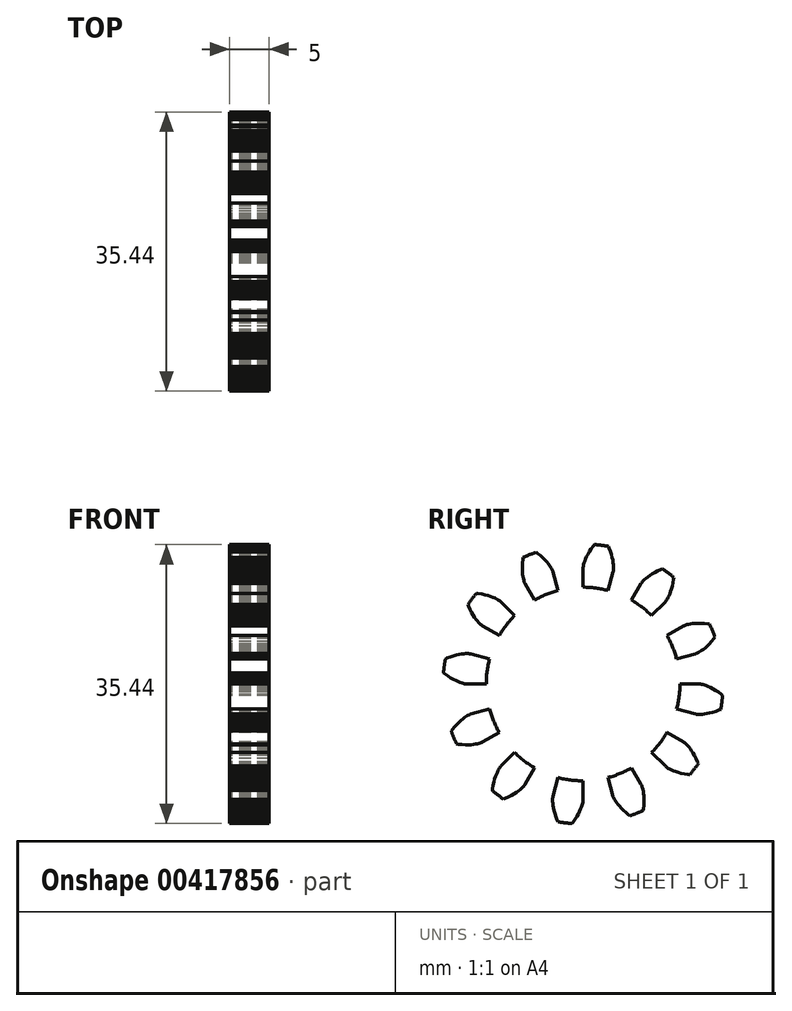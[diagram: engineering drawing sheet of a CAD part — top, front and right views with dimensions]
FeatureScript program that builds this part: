
annotation { "Feature Type Name" : "Feature", "Feature Type Description" : "" }
export const myFeature = defineFeature(function(context is Context, id is Id, definition is map)
    precondition{}
    {
        {
            assignVariable(context, id + "F0", {"name" : "GearThickness", "anyValue" : 5});
        }
        {
            var Q0;
            Q0=qCreatedBy(makeId("Right.planeOp"),FACE);
            var sketch = newSketch(context, id + "F1", { "sketchPlane" : qUnion([Q0])});
            skCircle(sketch, "E0", {"center": v(0, 0) * mm, "radius": 12.3 * mm});
            skCircle(sketch, "E1", {"center": v(0, 0) * mm, "radius": 14.75 * mm, "construction": true});
            skCircle(sketch, "E2", {"center": v(0, 0) * mm, "radius": 15.24 * mm, "construction": true});
            skCircle(sketch, "E3", {"center": v(0, 0) * mm, "radius": 17.78 * mm});
            skLineSegment(sketch, "E4", {"start": v(0, 0) * mm, "end": v(-14.75, 0) * mm, "construction": true});
            skLineSegment(sketch, "E5.1.0", {"start": v(0, 0) * mm, "end": v(-14.74, 0.74) * mm, "construction": true});
            skLineSegment(sketch, "E5.2.0", {"start": v(0, 0) * mm, "end": v(-14.68, 1.47) * mm, "construction": true});
            skLineSegment(sketch, "E5.3.0", {"start": v(0, 0) * mm, "end": v(-14.59, 2.2) * mm, "construction": true});
            skLineSegment(sketch, "E5.4.0", {"start": v(0, 0) * mm, "end": v(-14.46, 2.93) * mm, "construction": true});
            skLineSegment(sketch, "E5.5.0", {"start": v(0, 0) * mm, "end": v(-14.3, 3.65) * mm, "construction": true});
            skLineSegment(sketch, "E5.6.0", {"start": v(0, 0) * mm, "end": v(-14.1, 4.36) * mm, "construction": true});
            skLineSegment(sketch, "E5.7.0", {"start": v(0, 0) * mm, "end": v(-13.86, 5.06) * mm, "construction": true});
            skLineSegment(sketch, "E5.8.0", {"start": v(0, 0) * mm, "end": v(-13.59, 5.75) * mm, "construction": true});
            skLineSegment(sketch, "E5.9.0", {"start": v(0, 0) * mm, "end": v(-13.29, 6.42) * mm, "construction": true});
            skLineSegment(sketch, "E5.10.0", {"start": v(0, 0) * mm, "end": v(-12.95, 7.07) * mm, "construction": true});
            skLineSegment(sketch, "E5.11.0", {"start": v(0, 0) * mm, "end": v(-12.58, 7.71) * mm, "construction": true});
            skLineSegment(sketch, "E5.12.0", {"start": v(0, 0) * mm, "end": v(-12.18, 8.33) * mm, "construction": true});
            skLineSegment(sketch, "E5.13.0", {"start": v(0, 0) * mm, "end": v(-11.75, 8.93) * mm, "construction": true});
            skLineSegment(sketch, "E5.14.0", {"start": v(0, 0) * mm, "end": v(-11.28, 9.5) * mm, "construction": true});
            skLineSegment(sketch, "E5.anchor2", {"start": v(0, 0) * mm, "end": v(-11.28, 9.5) * mm, "construction": true});
            skLineSegment(sketch, "E6", {"start": v(-14.74, 0.74) * mm, "end": v(-14.77, 0) * mm, "construction": true});
            skLineSegment(sketch, "E7", {"start": v(-14.68, 1.47) * mm, "end": v(-14.83, 0) * mm, "construction": true});
            skLineSegment(sketch, "E8", {"start": v(-14.59, 2.2) * mm, "end": v(-14.92, 0.02) * mm, "construction": true});
            skLineSegment(sketch, "E9", {"start": v(-14.3, 3.65) * mm, "end": v(-15.2, 0.08) * mm, "construction": true});
            skLineSegment(sketch, "E10", {"start": v(-14.1, 4.36) * mm, "end": v(-15.4, 0.13) * mm, "construction": true});
            skLineSegment(sketch, "E11", {"start": v(-13.86, 5.06) * mm, "end": v(-15.63, 0.2) * mm, "construction": true});
            skLineSegment(sketch, "E12", {"start": v(-13.59, 5.75) * mm, "end": v(-15.89, 0.3) * mm, "construction": true});
            skLineSegment(sketch, "E13", {"start": v(-13.29, 6.42) * mm, "end": v(-16.17, 0.44) * mm, "construction": true});
            skLineSegment(sketch, "E14", {"start": v(-12.95, 7.07) * mm, "end": v(-16.49, 0.6) * mm, "construction": true});
            skLineSegment(sketch, "E15", {"start": v(-12.58, 7.71) * mm, "end": v(-16.82, 0.8) * mm, "construction": true});
            skLineSegment(sketch, "E16", {"start": v(-14.46, 2.93) * mm, "end": v(-15.05, 0.04) * mm, "construction": true});
            skLineSegment(sketch, "E17", {"start": v(-12.18, 8.33) * mm, "end": v(-17.18, 1.02) * mm, "construction": true});
            skLineSegment(sketch, "E18", {"start": v(-11.75, 8.93) * mm, "end": v(-17.55, 1.3) * mm, "construction": true});
            skLineSegment(sketch, "E19", {"start": v(-11.28, 9.5) * mm, "end": v(-17.94, 1.6) * mm, "construction": true});
            skLineSegment(sketch, "E20", {"start": v(0, 0) * mm, "end": v(-14.63, 1.93) * mm, "construction": true});
            skLineSegment(sketch, "E21", {"start": v(-12.3, 0) * mm, "end": v(-14.75, 0) * mm});
            skLineSegment(sketch, "E22.MirrorCS", {"start": v(-11.88, 3.18) * mm, "end": v(-14.25, 3.82) * mm});
            skLineSegment(sketch, "E23", {"start": v(-14.75, 0) * mm, "end": v(-14.77, 0) * mm});
            skLineSegment(sketch, "E24", {"start": v(-14.77, 0) * mm, "end": v(-14.83, 0) * mm});
            skLineSegment(sketch, "E25", {"start": v(-14.83, 0) * mm, "end": v(-14.92, 0.02) * mm});
            skLineSegment(sketch, "E26", {"start": v(-14.92, 0.02) * mm, "end": v(-15.05, 0.04) * mm});
            skLineSegment(sketch, "E27", {"start": v(-15.05, 0.04) * mm, "end": v(-15.2, 0.08) * mm});
            skLineSegment(sketch, "E28", {"start": v(-15.2, 0.08) * mm, "end": v(-15.4, 0.13) * mm});
            skLineSegment(sketch, "E29", {"start": v(-15.4, 0.13) * mm, "end": v(-15.63, 0.2) * mm});
            skLineSegment(sketch, "E30", {"start": v(-15.63, 0.2) * mm, "end": v(-15.89, 0.3) * mm});
            skLineSegment(sketch, "E31", {"start": v(-15.89, 0.3) * mm, "end": v(-16.17, 0.44) * mm});
            skLineSegment(sketch, "E32", {"start": v(-16.17, 0.44) * mm, "end": v(-16.49, 0.6) * mm});
            skLineSegment(sketch, "E33", {"start": v(-16.49, 0.6) * mm, "end": v(-16.82, 0.8) * mm});
            skLineSegment(sketch, "E34", {"start": v(-16.82, 0.8) * mm, "end": v(-17.18, 1.02) * mm});
            skLineSegment(sketch, "E35", {"start": v(-17.18, 1.02) * mm, "end": v(-17.55, 1.3) * mm});
            skLineSegment(sketch, "E36", {"start": v(-17.55, 1.3) * mm, "end": v(-17.94, 1.6) * mm});
            skLineSegment(sketch, "E37.MirrorCS", {"start": v(-14.25, 3.82) * mm, "end": v(-14.27, 3.82) * mm});
            skLineSegment(sketch, "E38.MirrorCS", {"start": v(-14.27, 3.82) * mm, "end": v(-14.32, 3.83) * mm});
            skLineSegment(sketch, "E39.MirrorCS", {"start": v(-14.32, 3.83) * mm, "end": v(-14.42, 3.85) * mm});
            skLineSegment(sketch, "E40.MirrorCS", {"start": v(-14.42, 3.85) * mm, "end": v(-14.54, 3.86) * mm});
            skLineSegment(sketch, "E41.MirrorCS", {"start": v(-14.71, 3.86) * mm, "end": v(-14.91, 3.86) * mm});
            skLineSegment(sketch, "E42.MirrorCS", {"start": v(-14.91, 3.86) * mm, "end": v(-15.15, 3.84) * mm});
            skLineSegment(sketch, "E43.MirrorCS", {"start": v(-15.15, 3.84) * mm, "end": v(-15.43, 3.81) * mm});
            skLineSegment(sketch, "E44.MirrorCS", {"start": v(-15.43, 3.81) * mm, "end": v(-15.74, 3.76) * mm});
            skLineSegment(sketch, "E45.MirrorCS", {"start": v(-16.08, 3.69) * mm, "end": v(-16.45, 3.59) * mm});
            skLineSegment(sketch, "E46.MirrorCS", {"start": v(-15.74, 3.76) * mm, "end": v(-16.08, 3.69) * mm});
            skLineSegment(sketch, "E47.MirrorCS", {"start": v(-16.45, 3.59) * mm, "end": v(-16.86, 3.46) * mm});
            skLineSegment(sketch, "E48.MirrorCS", {"start": v(-16.86, 3.46) * mm, "end": v(-17.29, 3.3) * mm});
            skLineSegment(sketch, "E49.MirrorCS", {"start": v(-17.29, 3.3) * mm, "end": v(-17.74, 3.1) * mm});
            skLineSegment(sketch, "E50.MirrorCS", {"start": v(-14.54, 3.86) * mm, "end": v(-14.71, 3.86) * mm});
            skLineSegment(sketch, "E51.1.0", {"start": v(-10.65, -6.15) * mm, "end": v(-12.78, -7.38) * mm});
            skLineSegment(sketch, "E51.1.1", {"start": v(-16.04, -5.12) * mm, "end": v(-16.33, -5.44) * mm});
            skLineSegment(sketch, "E51.1.2", {"start": v(-11.88, -3.18) * mm, "end": v(-14.25, -3.82) * mm});
            skLineSegment(sketch, "E51.1.3", {"start": v(-15.77, -4.85) * mm, "end": v(-16.04, -5.12) * mm});
            skLineSegment(sketch, "E51.1.4", {"start": v(-14.58, -7.72) * mm, "end": v(-14.96, -7.72) * mm});
            skLineSegment(sketch, "E51.1.5", {"start": v(-14.96, -7.72) * mm, "end": v(-15.39, -7.7) * mm});
            skLineSegment(sketch, "E51.1.6", {"start": v(-15.5, -4.61) * mm, "end": v(-15.77, -4.85) * mm});
            skLineSegment(sketch, "E51.1.7", {"start": v(-16.62, -5.8) * mm, "end": v(-16.91, -6.2) * mm});
            skLineSegment(sketch, "E51.1.8", {"start": v(-15.27, -4.41) * mm, "end": v(-15.5, -4.61) * mm});
            skLineSegment(sketch, "E51.1.9", {"start": v(-15.85, -7.65) * mm, "end": v(-16.34, -7.58) * mm});
            skLineSegment(sketch, "E51.1.10", {"start": v(-16.33, -5.44) * mm, "end": v(-16.62, -5.8) * mm});
            skLineSegment(sketch, "E51.1.11", {"start": v(-14.23, -7.7) * mm, "end": v(-14.58, -7.72) * mm});
            skLineSegment(sketch, "E51.1.12", {"start": v(-15.39, -7.7) * mm, "end": v(-15.85, -7.65) * mm});
            skLineSegment(sketch, "E51.1.13", {"start": v(-14.67, -4.01) * mm, "end": v(-14.84, -4.11) * mm});
            skLineSegment(sketch, "E51.1.14", {"start": v(-14.84, -4.11) * mm, "end": v(-15.04, -4.25) * mm});
            skLineSegment(sketch, "E51.1.15", {"start": v(-15.04, -4.25) * mm, "end": v(-15.27, -4.41) * mm});
            skLineSegment(sketch, "E51.1.16", {"start": v(-13.64, -7.64) * mm, "end": v(-13.91, -7.68) * mm});
            skLineSegment(sketch, "E51.1.17", {"start": v(-13.4, -7.59) * mm, "end": v(-13.64, -7.64) * mm});
            skLineSegment(sketch, "E51.1.18", {"start": v(-13.91, -7.68) * mm, "end": v(-14.23, -7.7) * mm});
            skLineSegment(sketch, "E51.1.19", {"start": v(-14.52, -3.93) * mm, "end": v(-14.67, -4.01) * mm});
            skLineSegment(sketch, "E51.1.20", {"start": v(-14.4, -3.88) * mm, "end": v(-14.52, -3.93) * mm});
            skLineSegment(sketch, "E51.1.21", {"start": v(-13.2, -7.54) * mm, "end": v(-13.4, -7.59) * mm});
            skLineSegment(sketch, "E51.1.22", {"start": v(-13.05, -7.49) * mm, "end": v(-13.2, -7.54) * mm});
            skLineSegment(sketch, "E51.1.23", {"start": v(-12.84, -7.4) * mm, "end": v(-12.93, -7.45) * mm});
            skLineSegment(sketch, "E51.1.24", {"start": v(-14.25, -3.82) * mm, "end": v(-14.27, -3.82) * mm});
            skLineSegment(sketch, "E51.1.25", {"start": v(-14.27, -3.82) * mm, "end": v(-14.32, -3.84) * mm});
            skLineSegment(sketch, "E51.1.26", {"start": v(-12.93, -7.45) * mm, "end": v(-13.05, -7.49) * mm});
            skLineSegment(sketch, "E51.1.27", {"start": v(-14.32, -3.84) * mm, "end": v(-14.4, -3.88) * mm});
            skLineSegment(sketch, "E51.1.28", {"start": v(-12.8, -7.39) * mm, "end": v(-12.84, -7.4) * mm});
            skLineSegment(sketch, "E51.1.29", {"start": v(-12.78, -7.38) * mm, "end": v(-12.8, -7.39) * mm});
            skLineSegment(sketch, "E51.2.0", {"start": v(-6.15, -10.65) * mm, "end": v(-7.38, -12.78) * mm});
            skLineSegment(sketch, "E51.2.1", {"start": v(-11.33, -12.45) * mm, "end": v(-11.42, -12.87) * mm});
            skLineSegment(sketch, "E51.2.2", {"start": v(-8.7, -8.7) * mm, "end": v(-10.43, -10.43) * mm});
            skLineSegment(sketch, "E51.2.3", {"start": v(-11.23, -12.08) * mm, "end": v(-11.33, -12.45) * mm});
            skLineSegment(sketch, "E51.2.4", {"start": v(-8.76, -13.98) * mm, "end": v(-9.1, -14.17) * mm});
            skLineSegment(sketch, "E51.2.5", {"start": v(-9.1, -14.17) * mm, "end": v(-9.48, -14.36) * mm});
            skLineSegment(sketch, "E51.2.6", {"start": v(-11.13, -11.75) * mm, "end": v(-11.23, -12.08) * mm});
            skLineSegment(sketch, "E51.2.7", {"start": v(-11.5, -13.32) * mm, "end": v(-11.55, -13.82) * mm});
            skLineSegment(sketch, "E51.2.8", {"start": v(-11.02, -11.45) * mm, "end": v(-11.13, -11.75) * mm});
            skLineSegment(sketch, "E51.2.9", {"start": v(-9.9, -14.55) * mm, "end": v(-10.36, -14.73) * mm});
            skLineSegment(sketch, "E51.2.10", {"start": v(-11.42, -12.87) * mm, "end": v(-11.5, -13.32) * mm});
            skLineSegment(sketch, "E51.2.11", {"start": v(-8.47, -13.79) * mm, "end": v(-8.76, -13.98) * mm});
            skLineSegment(sketch, "E51.2.12", {"start": v(-9.48, -14.36) * mm, "end": v(-9.9, -14.55) * mm});
            skLineSegment(sketch, "E51.2.13", {"start": v(-10.7, -10.8) * mm, "end": v(-10.8, -10.99) * mm});
            skLineSegment(sketch, "E51.2.14", {"start": v(-10.8, -10.99) * mm, "end": v(-10.9, -11.2) * mm});
            skLineSegment(sketch, "E51.2.15", {"start": v(-10.9, -11.2) * mm, "end": v(-11.02, -11.45) * mm});
            skLineSegment(sketch, "E51.2.16", {"start": v(-8, -13.43) * mm, "end": v(-8.21, -13.6) * mm});
            skLineSegment(sketch, "E51.2.17", {"start": v(-7.82, -13.27) * mm, "end": v(-8, -13.43) * mm});
            skLineSegment(sketch, "E51.2.18", {"start": v(-8.21, -13.6) * mm, "end": v(-8.47, -13.79) * mm});
            skLineSegment(sketch, "E51.2.19", {"start": v(-10.61, -10.67) * mm, "end": v(-10.7, -10.8) * mm});
            skLineSegment(sketch, "E51.2.20", {"start": v(-10.54, -10.56) * mm, "end": v(-10.61, -10.67) * mm});
            skLineSegment(sketch, "E51.2.21", {"start": v(-7.67, -13.13) * mm, "end": v(-7.82, -13.27) * mm});
            skLineSegment(sketch, "E51.2.22", {"start": v(-7.56, -13.01) * mm, "end": v(-7.67, -13.13) * mm});
            skLineSegment(sketch, "E51.2.23", {"start": v(-7.42, -12.84) * mm, "end": v(-7.47, -12.91) * mm});
            skLineSegment(sketch, "E51.2.24", {"start": v(-10.43, -10.43) * mm, "end": v(-10.45, -10.45) * mm});
            skLineSegment(sketch, "E51.2.25", {"start": v(-10.45, -10.45) * mm, "end": v(-10.48, -10.49) * mm});
            skLineSegment(sketch, "E51.2.26", {"start": v(-7.47, -12.91) * mm, "end": v(-7.56, -13.01) * mm});
            skLineSegment(sketch, "E51.2.27", {"start": v(-10.48, -10.49) * mm, "end": v(-10.54, -10.56) * mm});
            skLineSegment(sketch, "E51.2.28", {"start": v(-7.39, -12.8) * mm, "end": v(-7.42, -12.84) * mm});
            skLineSegment(sketch, "E51.2.29", {"start": v(-7.38, -12.78) * mm, "end": v(-7.39, -12.8) * mm});
            skLineSegment(sketch, "E51.3.0", {"start": v(0, -12.3) * mm, "end": v(0, -14.75) * mm});
            skLineSegment(sketch, "E51.3.1", {"start": v(-3.59, -16.45) * mm, "end": v(-3.46, -16.86) * mm});
            skLineSegment(sketch, "E51.3.2", {"start": v(-3.18, -11.88) * mm, "end": v(-3.82, -14.25) * mm});
            skLineSegment(sketch, "E51.3.3", {"start": v(-3.69, -16.08) * mm, "end": v(-3.59, -16.45) * mm});
            skLineSegment(sketch, "E51.3.4", {"start": v(-0.6, -16.49) * mm, "end": v(-0.8, -16.82) * mm});
            skLineSegment(sketch, "E51.3.5", {"start": v(-0.8, -16.82) * mm, "end": v(-1.02, -17.18) * mm});
            skLineSegment(sketch, "E51.3.6", {"start": v(-3.76, -15.74) * mm, "end": v(-3.69, -16.08) * mm});
            skLineSegment(sketch, "E51.3.7", {"start": v(-3.3, -17.29) * mm, "end": v(-3.1, -17.74) * mm});
            skLineSegment(sketch, "E51.3.8", {"start": v(-3.81, -15.43) * mm, "end": v(-3.76, -15.74) * mm});
            skLineSegment(sketch, "E51.3.9", {"start": v(-1.3, -17.55) * mm, "end": v(-1.6, -17.94) * mm});
            skLineSegment(sketch, "E51.3.10", {"start": v(-3.46, -16.86) * mm, "end": v(-3.3, -17.29) * mm});
            skLineSegment(sketch, "E51.3.11", {"start": v(-0.44, -16.17) * mm, "end": v(-0.6, -16.49) * mm});
            skLineSegment(sketch, "E51.3.12", {"start": v(-1.02, -17.18) * mm, "end": v(-1.3, -17.55) * mm});
            skLineSegment(sketch, "E51.3.13", {"start": v(-3.86, -14.71) * mm, "end": v(-3.86, -14.91) * mm});
            skLineSegment(sketch, "E51.3.14", {"start": v(-3.86, -14.91) * mm, "end": v(-3.84, -15.15) * mm});
            skLineSegment(sketch, "E51.3.15", {"start": v(-3.84, -15.15) * mm, "end": v(-3.81, -15.43) * mm});
            skLineSegment(sketch, "E51.3.16", {"start": v(-0.2, -15.63) * mm, "end": v(-0.3, -15.89) * mm});
            skLineSegment(sketch, "E51.3.17", {"start": v(-0.13, -15.4) * mm, "end": v(-0.2, -15.63) * mm});
            skLineSegment(sketch, "E51.3.18", {"start": v(-0.3, -15.89) * mm, "end": v(-0.44, -16.17) * mm});
            skLineSegment(sketch, "E51.3.19", {"start": v(-3.86, -14.54) * mm, "end": v(-3.86, -14.71) * mm});
            skLineSegment(sketch, "E51.3.20", {"start": v(-3.85, -14.42) * mm, "end": v(-3.86, -14.54) * mm});
            skLineSegment(sketch, "E51.3.21", {"start": v(-0.08, -15.2) * mm, "end": v(-0.13, -15.4) * mm});
            skLineSegment(sketch, "E51.3.22", {"start": v(-0.04, -15.05) * mm, "end": v(-0.08, -15.2) * mm});
            skLineSegment(sketch, "E51.3.23", {"start": v(0, -14.83) * mm, "end": v(-0.02, -14.92) * mm});
            skLineSegment(sketch, "E51.3.24", {"start": v(-3.82, -14.25) * mm, "end": v(-3.82, -14.27) * mm});
            skLineSegment(sketch, "E51.3.25", {"start": v(-3.82, -14.27) * mm, "end": v(-3.83, -14.32) * mm});
            skLineSegment(sketch, "E51.3.26", {"start": v(-0.02, -14.92) * mm, "end": v(-0.04, -15.05) * mm});
            skLineSegment(sketch, "E51.3.27", {"start": v(-3.83, -14.32) * mm, "end": v(-3.85, -14.42) * mm});
            skLineSegment(sketch, "E51.3.28", {"start": v(0, -14.77) * mm, "end": v(0, -14.83) * mm});
            skLineSegment(sketch, "E51.3.29", {"start": v(0, -14.75) * mm, "end": v(0, -14.77) * mm});
            skLineSegment(sketch, "E51.4.0", {"start": v(6.15, -10.65) * mm, "end": v(7.38, -12.78) * mm});
            skLineSegment(sketch, "E51.4.1", {"start": v(5.12, -16.04) * mm, "end": v(5.44, -16.33) * mm});
            skLineSegment(sketch, "E51.4.2", {"start": v(3.18, -11.88) * mm, "end": v(3.82, -14.25) * mm});
            skLineSegment(sketch, "E51.4.3", {"start": v(4.85, -15.77) * mm, "end": v(5.12, -16.04) * mm});
            skLineSegment(sketch, "E51.4.4", {"start": v(7.72, -14.58) * mm, "end": v(7.72, -14.96) * mm});
            skLineSegment(sketch, "E51.4.5", {"start": v(7.72, -14.96) * mm, "end": v(7.7, -15.39) * mm});
            skLineSegment(sketch, "E51.4.6", {"start": v(4.61, -15.5) * mm, "end": v(4.85, -15.77) * mm});
            skLineSegment(sketch, "E51.4.7", {"start": v(5.8, -16.62) * mm, "end": v(6.2, -16.91) * mm});
            skLineSegment(sketch, "E51.4.8", {"start": v(4.41, -15.27) * mm, "end": v(4.61, -15.5) * mm});
            skLineSegment(sketch, "E51.4.9", {"start": v(7.65, -15.85) * mm, "end": v(7.58, -16.34) * mm});
            skLineSegment(sketch, "E51.4.10", {"start": v(5.44, -16.33) * mm, "end": v(5.8, -16.62) * mm});
            skLineSegment(sketch, "E51.4.11", {"start": v(7.7, -14.23) * mm, "end": v(7.72, -14.58) * mm});
            skLineSegment(sketch, "E51.4.12", {"start": v(7.7, -15.39) * mm, "end": v(7.65, -15.85) * mm});
            skLineSegment(sketch, "E51.4.13", {"start": v(4.01, -14.67) * mm, "end": v(4.11, -14.84) * mm});
            skLineSegment(sketch, "E51.4.14", {"start": v(4.11, -14.84) * mm, "end": v(4.25, -15.04) * mm});
            skLineSegment(sketch, "E51.4.15", {"start": v(4.25, -15.04) * mm, "end": v(4.41, -15.27) * mm});
            skLineSegment(sketch, "E51.4.16", {"start": v(7.64, -13.64) * mm, "end": v(7.68, -13.91) * mm});
            skLineSegment(sketch, "E51.4.17", {"start": v(7.59, -13.4) * mm, "end": v(7.64, -13.64) * mm});
            skLineSegment(sketch, "E51.4.18", {"start": v(7.68, -13.91) * mm, "end": v(7.7, -14.23) * mm});
            skLineSegment(sketch, "E51.4.19", {"start": v(3.93, -14.52) * mm, "end": v(4.01, -14.67) * mm});
            skLineSegment(sketch, "E51.4.20", {"start": v(3.88, -14.4) * mm, "end": v(3.93, -14.52) * mm});
            skLineSegment(sketch, "E51.4.21", {"start": v(7.54, -13.2) * mm, "end": v(7.59, -13.4) * mm});
            skLineSegment(sketch, "E51.4.22", {"start": v(7.49, -13.05) * mm, "end": v(7.54, -13.2) * mm});
            skLineSegment(sketch, "E51.4.23", {"start": v(7.4, -12.84) * mm, "end": v(7.45, -12.93) * mm});
            skLineSegment(sketch, "E51.4.24", {"start": v(3.82, -14.25) * mm, "end": v(3.82, -14.27) * mm});
            skLineSegment(sketch, "E51.4.25", {"start": v(3.82, -14.27) * mm, "end": v(3.84, -14.32) * mm});
            skLineSegment(sketch, "E51.4.26", {"start": v(7.45, -12.93) * mm, "end": v(7.49, -13.05) * mm});
            skLineSegment(sketch, "E51.4.27", {"start": v(3.84, -14.32) * mm, "end": v(3.88, -14.4) * mm});
            skLineSegment(sketch, "E51.4.28", {"start": v(7.39, -12.8) * mm, "end": v(7.4, -12.84) * mm});
            skLineSegment(sketch, "E51.4.29", {"start": v(7.38, -12.78) * mm, "end": v(7.39, -12.8) * mm});
            skLineSegment(sketch, "E51.5.0", {"start": v(10.65, -6.15) * mm, "end": v(12.78, -7.38) * mm});
            skLineSegment(sketch, "E51.5.1", {"start": v(12.45, -11.33) * mm, "end": v(12.87, -11.42) * mm});
            skLineSegment(sketch, "E51.5.2", {"start": v(8.7, -8.7) * mm, "end": v(10.43, -10.43) * mm});
            skLineSegment(sketch, "E51.5.3", {"start": v(12.08, -11.23) * mm, "end": v(12.45, -11.33) * mm});
            skLineSegment(sketch, "E51.5.4", {"start": v(13.98, -8.76) * mm, "end": v(14.17, -9.1) * mm});
            skLineSegment(sketch, "E51.5.5", {"start": v(14.17, -9.1) * mm, "end": v(14.36, -9.48) * mm});
            skLineSegment(sketch, "E51.5.6", {"start": v(11.75, -11.13) * mm, "end": v(12.08, -11.23) * mm});
            skLineSegment(sketch, "E51.5.7", {"start": v(13.32, -11.5) * mm, "end": v(13.82, -11.55) * mm});
            skLineSegment(sketch, "E51.5.8", {"start": v(11.45, -11.02) * mm, "end": v(11.75, -11.13) * mm});
            skLineSegment(sketch, "E51.5.9", {"start": v(14.55, -9.9) * mm, "end": v(14.73, -10.36) * mm});
            skLineSegment(sketch, "E51.5.10", {"start": v(12.87, -11.42) * mm, "end": v(13.32, -11.5) * mm});
            skLineSegment(sketch, "E51.5.11", {"start": v(13.79, -8.47) * mm, "end": v(13.98, -8.76) * mm});
            skLineSegment(sketch, "E51.5.12", {"start": v(14.36, -9.48) * mm, "end": v(14.55, -9.9) * mm});
            skLineSegment(sketch, "E51.5.13", {"start": v(10.8, -10.7) * mm, "end": v(10.99, -10.8) * mm});
            skLineSegment(sketch, "E51.5.14", {"start": v(10.99, -10.8) * mm, "end": v(11.2, -10.9) * mm});
            skLineSegment(sketch, "E51.5.15", {"start": v(11.2, -10.9) * mm, "end": v(11.45, -11.02) * mm});
            skLineSegment(sketch, "E51.5.16", {"start": v(13.43, -8) * mm, "end": v(13.6, -8.21) * mm});
            skLineSegment(sketch, "E51.5.17", {"start": v(13.27, -7.82) * mm, "end": v(13.43, -8) * mm});
            skLineSegment(sketch, "E51.5.18", {"start": v(13.6, -8.21) * mm, "end": v(13.79, -8.47) * mm});
            skLineSegment(sketch, "E51.5.19", {"start": v(10.67, -10.61) * mm, "end": v(10.8, -10.7) * mm});
            skLineSegment(sketch, "E51.5.20", {"start": v(10.56, -10.54) * mm, "end": v(10.67, -10.61) * mm});
            skLineSegment(sketch, "E51.5.21", {"start": v(13.13, -7.67) * mm, "end": v(13.27, -7.82) * mm});
            skLineSegment(sketch, "E51.5.22", {"start": v(13.01, -7.56) * mm, "end": v(13.13, -7.67) * mm});
            skLineSegment(sketch, "E51.5.23", {"start": v(12.84, -7.42) * mm, "end": v(12.91, -7.47) * mm});
            skLineSegment(sketch, "E51.5.24", {"start": v(10.43, -10.43) * mm, "end": v(10.45, -10.45) * mm});
            skLineSegment(sketch, "E51.5.25", {"start": v(10.45, -10.45) * mm, "end": v(10.49, -10.48) * mm});
            skLineSegment(sketch, "E51.5.26", {"start": v(12.91, -7.47) * mm, "end": v(13.01, -7.56) * mm});
            skLineSegment(sketch, "E51.5.27", {"start": v(10.49, -10.48) * mm, "end": v(10.56, -10.54) * mm});
            skLineSegment(sketch, "E51.5.28", {"start": v(12.8, -7.39) * mm, "end": v(12.84, -7.42) * mm});
            skLineSegment(sketch, "E51.5.29", {"start": v(12.78, -7.38) * mm, "end": v(12.8, -7.39) * mm});
            skLineSegment(sketch, "E51.6.0", {"start": v(12.3, 0) * mm, "end": v(14.75, 0) * mm});
            skLineSegment(sketch, "E51.6.1", {"start": v(16.45, -3.59) * mm, "end": v(16.86, -3.46) * mm});
            skLineSegment(sketch, "E51.6.2", {"start": v(11.88, -3.18) * mm, "end": v(14.25, -3.82) * mm});
            skLineSegment(sketch, "E51.6.3", {"start": v(16.08, -3.69) * mm, "end": v(16.45, -3.59) * mm});
            skLineSegment(sketch, "E51.6.4", {"start": v(16.49, -0.6) * mm, "end": v(16.82, -0.8) * mm});
            skLineSegment(sketch, "E51.6.5", {"start": v(16.82, -0.8) * mm, "end": v(17.18, -1.02) * mm});
            skLineSegment(sketch, "E51.6.6", {"start": v(15.74, -3.76) * mm, "end": v(16.08, -3.69) * mm});
            skLineSegment(sketch, "E51.6.7", {"start": v(17.29, -3.3) * mm, "end": v(17.74, -3.1) * mm});
            skLineSegment(sketch, "E51.6.8", {"start": v(15.43, -3.81) * mm, "end": v(15.74, -3.76) * mm});
            skLineSegment(sketch, "E51.6.9", {"start": v(17.55, -1.3) * mm, "end": v(17.94, -1.6) * mm});
            skLineSegment(sketch, "E51.6.10", {"start": v(16.86, -3.46) * mm, "end": v(17.29, -3.3) * mm});
            skLineSegment(sketch, "E51.6.11", {"start": v(16.17, -0.44) * mm, "end": v(16.49, -0.6) * mm});
            skLineSegment(sketch, "E51.6.12", {"start": v(17.18, -1.02) * mm, "end": v(17.55, -1.3) * mm});
            skLineSegment(sketch, "E51.6.13", {"start": v(14.71, -3.86) * mm, "end": v(14.91, -3.86) * mm});
            skLineSegment(sketch, "E51.6.14", {"start": v(14.91, -3.86) * mm, "end": v(15.15, -3.84) * mm});
            skLineSegment(sketch, "E51.6.15", {"start": v(15.15, -3.84) * mm, "end": v(15.43, -3.81) * mm});
            skLineSegment(sketch, "E51.6.16", {"start": v(15.63, -0.2) * mm, "end": v(15.89, -0.3) * mm});
            skLineSegment(sketch, "E51.6.17", {"start": v(15.4, -0.13) * mm, "end": v(15.63, -0.2) * mm});
            skLineSegment(sketch, "E51.6.18", {"start": v(15.89, -0.3) * mm, "end": v(16.17, -0.44) * mm});
            skLineSegment(sketch, "E51.6.19", {"start": v(14.54, -3.86) * mm, "end": v(14.71, -3.86) * mm});
            skLineSegment(sketch, "E51.6.20", {"start": v(14.42, -3.85) * mm, "end": v(14.54, -3.86) * mm});
            skLineSegment(sketch, "E51.6.21", {"start": v(15.2, -0.08) * mm, "end": v(15.4, -0.13) * mm});
            skLineSegment(sketch, "E51.6.22", {"start": v(15.05, -0.04) * mm, "end": v(15.2, -0.08) * mm});
            skLineSegment(sketch, "E51.6.23", {"start": v(14.83, 0) * mm, "end": v(14.92, -0.02) * mm});
            skLineSegment(sketch, "E51.6.24", {"start": v(14.25, -3.82) * mm, "end": v(14.27, -3.82) * mm});
            skLineSegment(sketch, "E51.6.25", {"start": v(14.27, -3.82) * mm, "end": v(14.32, -3.83) * mm});
            skLineSegment(sketch, "E51.6.26", {"start": v(14.92, -0.02) * mm, "end": v(15.05, -0.04) * mm});
            skLineSegment(sketch, "E51.6.27", {"start": v(14.32, -3.83) * mm, "end": v(14.42, -3.85) * mm});
            skLineSegment(sketch, "E51.6.28", {"start": v(14.77, 0) * mm, "end": v(14.83, 0) * mm});
            skLineSegment(sketch, "E51.6.29", {"start": v(14.75, 0) * mm, "end": v(14.77, 0) * mm});
            skLineSegment(sketch, "E51.7.0", {"start": v(10.65, 6.15) * mm, "end": v(12.78, 7.38) * mm});
            skLineSegment(sketch, "E51.7.1", {"start": v(16.04, 5.12) * mm, "end": v(16.33, 5.44) * mm});
            skLineSegment(sketch, "E51.7.2", {"start": v(11.88, 3.18) * mm, "end": v(14.25, 3.82) * mm});
            skLineSegment(sketch, "E51.7.3", {"start": v(15.77, 4.85) * mm, "end": v(16.04, 5.12) * mm});
            skLineSegment(sketch, "E51.7.4", {"start": v(14.58, 7.72) * mm, "end": v(14.96, 7.72) * mm});
            skLineSegment(sketch, "E51.7.5", {"start": v(14.96, 7.72) * mm, "end": v(15.39, 7.7) * mm});
            skLineSegment(sketch, "E51.7.6", {"start": v(15.5, 4.61) * mm, "end": v(15.77, 4.85) * mm});
            skLineSegment(sketch, "E51.7.7", {"start": v(16.62, 5.8) * mm, "end": v(16.91, 6.2) * mm});
            skLineSegment(sketch, "E51.7.8", {"start": v(15.27, 4.41) * mm, "end": v(15.5, 4.61) * mm});
            skLineSegment(sketch, "E51.7.9", {"start": v(15.85, 7.65) * mm, "end": v(16.34, 7.58) * mm});
            skLineSegment(sketch, "E51.7.10", {"start": v(16.33, 5.44) * mm, "end": v(16.62, 5.8) * mm});
            skLineSegment(sketch, "E51.7.11", {"start": v(14.23, 7.7) * mm, "end": v(14.58, 7.72) * mm});
            skLineSegment(sketch, "E51.7.12", {"start": v(15.39, 7.7) * mm, "end": v(15.85, 7.65) * mm});
            skLineSegment(sketch, "E51.7.13", {"start": v(14.67, 4.01) * mm, "end": v(14.84, 4.11) * mm});
            skLineSegment(sketch, "E51.7.14", {"start": v(14.84, 4.11) * mm, "end": v(15.04, 4.25) * mm});
            skLineSegment(sketch, "E51.7.15", {"start": v(15.04, 4.25) * mm, "end": v(15.27, 4.41) * mm});
            skLineSegment(sketch, "E51.7.16", {"start": v(13.64, 7.64) * mm, "end": v(13.91, 7.68) * mm});
            skLineSegment(sketch, "E51.7.17", {"start": v(13.4, 7.59) * mm, "end": v(13.64, 7.64) * mm});
            skLineSegment(sketch, "E51.7.18", {"start": v(13.91, 7.68) * mm, "end": v(14.23, 7.7) * mm});
            skLineSegment(sketch, "E51.7.19", {"start": v(14.52, 3.93) * mm, "end": v(14.67, 4.01) * mm});
            skLineSegment(sketch, "E51.7.20", {"start": v(14.4, 3.88) * mm, "end": v(14.52, 3.93) * mm});
            skLineSegment(sketch, "E51.7.21", {"start": v(13.2, 7.54) * mm, "end": v(13.4, 7.59) * mm});
            skLineSegment(sketch, "E51.7.22", {"start": v(13.05, 7.49) * mm, "end": v(13.2, 7.54) * mm});
            skLineSegment(sketch, "E51.7.23", {"start": v(12.84, 7.4) * mm, "end": v(12.93, 7.45) * mm});
            skLineSegment(sketch, "E51.7.24", {"start": v(14.25, 3.82) * mm, "end": v(14.27, 3.82) * mm});
            skLineSegment(sketch, "E51.7.25", {"start": v(14.27, 3.82) * mm, "end": v(14.32, 3.84) * mm});
            skLineSegment(sketch, "E51.7.26", {"start": v(12.93, 7.45) * mm, "end": v(13.05, 7.49) * mm});
            skLineSegment(sketch, "E51.7.27", {"start": v(14.32, 3.84) * mm, "end": v(14.4, 3.88) * mm});
            skLineSegment(sketch, "E51.7.28", {"start": v(12.8, 7.39) * mm, "end": v(12.84, 7.4) * mm});
            skLineSegment(sketch, "E51.7.29", {"start": v(12.78, 7.38) * mm, "end": v(12.8, 7.39) * mm});
            skLineSegment(sketch, "E51.8.0", {"start": v(6.15, 10.65) * mm, "end": v(7.38, 12.78) * mm});
            skLineSegment(sketch, "E51.8.1", {"start": v(11.33, 12.45) * mm, "end": v(11.42, 12.87) * mm});
            skLineSegment(sketch, "E51.8.2", {"start": v(8.7, 8.7) * mm, "end": v(10.43, 10.43) * mm});
            skLineSegment(sketch, "E51.8.3", {"start": v(11.23, 12.08) * mm, "end": v(11.33, 12.45) * mm});
            skLineSegment(sketch, "E51.8.4", {"start": v(8.76, 13.98) * mm, "end": v(9.1, 14.17) * mm});
            skLineSegment(sketch, "E51.8.5", {"start": v(9.1, 14.17) * mm, "end": v(9.48, 14.36) * mm});
            skLineSegment(sketch, "E51.8.6", {"start": v(11.13, 11.75) * mm, "end": v(11.23, 12.08) * mm});
            skLineSegment(sketch, "E51.8.7", {"start": v(11.5, 13.32) * mm, "end": v(11.55, 13.82) * mm});
            skLineSegment(sketch, "E51.8.8", {"start": v(11.02, 11.45) * mm, "end": v(11.13, 11.75) * mm});
            skLineSegment(sketch, "E51.8.9", {"start": v(9.9, 14.55) * mm, "end": v(10.36, 14.73) * mm});
            skLineSegment(sketch, "E51.8.10", {"start": v(11.42, 12.87) * mm, "end": v(11.5, 13.32) * mm});
            skLineSegment(sketch, "E51.8.11", {"start": v(8.47, 13.79) * mm, "end": v(8.76, 13.98) * mm});
            skLineSegment(sketch, "E51.8.12", {"start": v(9.48, 14.36) * mm, "end": v(9.9, 14.55) * mm});
            skLineSegment(sketch, "E51.8.13", {"start": v(10.7, 10.8) * mm, "end": v(10.8, 10.99) * mm});
            skLineSegment(sketch, "E51.8.14", {"start": v(10.8, 10.99) * mm, "end": v(10.9, 11.2) * mm});
            skLineSegment(sketch, "E51.8.15", {"start": v(10.9, 11.2) * mm, "end": v(11.02, 11.45) * mm});
            skLineSegment(sketch, "E51.8.16", {"start": v(8, 13.43) * mm, "end": v(8.21, 13.6) * mm});
            skLineSegment(sketch, "E51.8.17", {"start": v(7.82, 13.27) * mm, "end": v(8, 13.43) * mm});
            skLineSegment(sketch, "E51.8.18", {"start": v(8.21, 13.6) * mm, "end": v(8.47, 13.79) * mm});
            skLineSegment(sketch, "E51.8.19", {"start": v(10.61, 10.67) * mm, "end": v(10.7, 10.8) * mm});
            skLineSegment(sketch, "E51.8.20", {"start": v(10.54, 10.56) * mm, "end": v(10.61, 10.67) * mm});
            skLineSegment(sketch, "E51.8.21", {"start": v(7.67, 13.13) * mm, "end": v(7.82, 13.27) * mm});
            skLineSegment(sketch, "E51.8.22", {"start": v(7.56, 13.01) * mm, "end": v(7.67, 13.13) * mm});
            skLineSegment(sketch, "E51.8.23", {"start": v(7.42, 12.84) * mm, "end": v(7.47, 12.91) * mm});
            skLineSegment(sketch, "E51.8.24", {"start": v(10.43, 10.43) * mm, "end": v(10.45, 10.45) * mm});
            skLineSegment(sketch, "E51.8.25", {"start": v(10.45, 10.45) * mm, "end": v(10.48, 10.49) * mm});
            skLineSegment(sketch, "E51.8.26", {"start": v(7.47, 12.91) * mm, "end": v(7.56, 13.01) * mm});
            skLineSegment(sketch, "E51.8.27", {"start": v(10.48, 10.49) * mm, "end": v(10.54, 10.56) * mm});
            skLineSegment(sketch, "E51.8.28", {"start": v(7.39, 12.8) * mm, "end": v(7.42, 12.84) * mm});
            skLineSegment(sketch, "E51.8.29", {"start": v(7.38, 12.78) * mm, "end": v(7.39, 12.8) * mm});
            skLineSegment(sketch, "E51.9.0", {"start": v(0, 12.3) * mm, "end": v(0, 14.75) * mm});
            skLineSegment(sketch, "E51.9.1", {"start": v(3.59, 16.45) * mm, "end": v(3.46, 16.86) * mm});
            skLineSegment(sketch, "E51.9.2", {"start": v(3.18, 11.88) * mm, "end": v(3.82, 14.25) * mm});
            skLineSegment(sketch, "E51.9.3", {"start": v(3.69, 16.08) * mm, "end": v(3.59, 16.45) * mm});
            skLineSegment(sketch, "E51.9.4", {"start": v(0.6, 16.49) * mm, "end": v(0.8, 16.82) * mm});
            skLineSegment(sketch, "E51.9.5", {"start": v(0.8, 16.82) * mm, "end": v(1.02, 17.18) * mm});
            skLineSegment(sketch, "E51.9.6", {"start": v(3.76, 15.74) * mm, "end": v(3.69, 16.08) * mm});
            skLineSegment(sketch, "E51.9.7", {"start": v(3.3, 17.29) * mm, "end": v(3.1, 17.74) * mm});
            skLineSegment(sketch, "E51.9.8", {"start": v(3.81, 15.43) * mm, "end": v(3.76, 15.74) * mm});
            skLineSegment(sketch, "E51.9.9", {"start": v(1.3, 17.55) * mm, "end": v(1.6, 17.94) * mm});
            skLineSegment(sketch, "E51.9.10", {"start": v(3.46, 16.86) * mm, "end": v(3.3, 17.29) * mm});
            skLineSegment(sketch, "E51.9.11", {"start": v(0.44, 16.17) * mm, "end": v(0.6, 16.49) * mm});
            skLineSegment(sketch, "E51.9.12", {"start": v(1.02, 17.18) * mm, "end": v(1.3, 17.55) * mm});
            skLineSegment(sketch, "E51.9.13", {"start": v(3.86, 14.71) * mm, "end": v(3.86, 14.91) * mm});
            skLineSegment(sketch, "E51.9.14", {"start": v(3.86, 14.91) * mm, "end": v(3.84, 15.15) * mm});
            skLineSegment(sketch, "E51.9.15", {"start": v(3.84, 15.15) * mm, "end": v(3.81, 15.43) * mm});
            skLineSegment(sketch, "E51.9.16", {"start": v(0.2, 15.63) * mm, "end": v(0.3, 15.89) * mm});
            skLineSegment(sketch, "E51.9.17", {"start": v(0.13, 15.4) * mm, "end": v(0.2, 15.63) * mm});
            skLineSegment(sketch, "E51.9.18", {"start": v(0.3, 15.89) * mm, "end": v(0.44, 16.17) * mm});
            skLineSegment(sketch, "E51.9.19", {"start": v(3.86, 14.54) * mm, "end": v(3.86, 14.71) * mm});
            skLineSegment(sketch, "E51.9.20", {"start": v(3.85, 14.42) * mm, "end": v(3.86, 14.54) * mm});
            skLineSegment(sketch, "E51.9.21", {"start": v(0.08, 15.2) * mm, "end": v(0.13, 15.4) * mm});
            skLineSegment(sketch, "E51.9.22", {"start": v(0.04, 15.05) * mm, "end": v(0.08, 15.2) * mm});
            skLineSegment(sketch, "E51.9.23", {"start": v(0, 14.83) * mm, "end": v(0.02, 14.92) * mm});
            skLineSegment(sketch, "E51.9.24", {"start": v(3.82, 14.25) * mm, "end": v(3.82, 14.27) * mm});
            skLineSegment(sketch, "E51.9.25", {"start": v(3.82, 14.27) * mm, "end": v(3.83, 14.32) * mm});
            skLineSegment(sketch, "E51.9.26", {"start": v(0.02, 14.92) * mm, "end": v(0.04, 15.05) * mm});
            skLineSegment(sketch, "E51.9.27", {"start": v(3.83, 14.32) * mm, "end": v(3.85, 14.42) * mm});
            skLineSegment(sketch, "E51.9.28", {"start": v(0, 14.77) * mm, "end": v(0, 14.83) * mm});
            skLineSegment(sketch, "E51.9.29", {"start": v(0, 14.75) * mm, "end": v(0, 14.77) * mm});
            skLineSegment(sketch, "E51.10.0", {"start": v(-6.15, 10.65) * mm, "end": v(-7.38, 12.78) * mm});
            skLineSegment(sketch, "E51.10.1", {"start": v(-5.12, 16.04) * mm, "end": v(-5.44, 16.33) * mm});
            skLineSegment(sketch, "E51.10.2", {"start": v(-3.18, 11.88) * mm, "end": v(-3.82, 14.25) * mm});
            skLineSegment(sketch, "E51.10.3", {"start": v(-4.85, 15.77) * mm, "end": v(-5.12, 16.04) * mm});
            skLineSegment(sketch, "E51.10.4", {"start": v(-7.72, 14.58) * mm, "end": v(-7.72, 14.96) * mm});
            skLineSegment(sketch, "E51.10.5", {"start": v(-7.72, 14.96) * mm, "end": v(-7.7, 15.39) * mm});
            skLineSegment(sketch, "E51.10.6", {"start": v(-4.61, 15.5) * mm, "end": v(-4.85, 15.77) * mm});
            skLineSegment(sketch, "E51.10.7", {"start": v(-5.8, 16.62) * mm, "end": v(-6.2, 16.91) * mm});
            skLineSegment(sketch, "E51.10.8", {"start": v(-4.41, 15.27) * mm, "end": v(-4.61, 15.5) * mm});
            skLineSegment(sketch, "E51.10.9", {"start": v(-7.65, 15.85) * mm, "end": v(-7.58, 16.34) * mm});
            skLineSegment(sketch, "E51.10.10", {"start": v(-5.44, 16.33) * mm, "end": v(-5.8, 16.62) * mm});
            skLineSegment(sketch, "E51.10.11", {"start": v(-7.7, 14.23) * mm, "end": v(-7.72, 14.58) * mm});
            skLineSegment(sketch, "E51.10.12", {"start": v(-7.7, 15.39) * mm, "end": v(-7.65, 15.85) * mm});
            skLineSegment(sketch, "E51.10.13", {"start": v(-4.01, 14.67) * mm, "end": v(-4.11, 14.84) * mm});
            skLineSegment(sketch, "E51.10.14", {"start": v(-4.11, 14.84) * mm, "end": v(-4.25, 15.04) * mm});
            skLineSegment(sketch, "E51.10.15", {"start": v(-4.25, 15.04) * mm, "end": v(-4.41, 15.27) * mm});
            skLineSegment(sketch, "E51.10.16", {"start": v(-7.64, 13.64) * mm, "end": v(-7.68, 13.91) * mm});
            skLineSegment(sketch, "E51.10.17", {"start": v(-7.59, 13.4) * mm, "end": v(-7.64, 13.64) * mm});
            skLineSegment(sketch, "E51.10.18", {"start": v(-7.68, 13.91) * mm, "end": v(-7.7, 14.23) * mm});
            skLineSegment(sketch, "E51.10.19", {"start": v(-3.93, 14.52) * mm, "end": v(-4.01, 14.67) * mm});
            skLineSegment(sketch, "E51.10.20", {"start": v(-3.88, 14.4) * mm, "end": v(-3.93, 14.52) * mm});
            skLineSegment(sketch, "E51.10.21", {"start": v(-7.54, 13.2) * mm, "end": v(-7.59, 13.4) * mm});
            skLineSegment(sketch, "E51.10.22", {"start": v(-7.49, 13.05) * mm, "end": v(-7.54, 13.2) * mm});
            skLineSegment(sketch, "E51.10.23", {"start": v(-7.4, 12.84) * mm, "end": v(-7.45, 12.93) * mm});
            skLineSegment(sketch, "E51.10.24", {"start": v(-3.82, 14.25) * mm, "end": v(-3.82, 14.27) * mm});
            skLineSegment(sketch, "E51.10.25", {"start": v(-3.82, 14.27) * mm, "end": v(-3.84, 14.32) * mm});
            skLineSegment(sketch, "E51.10.26", {"start": v(-7.45, 12.93) * mm, "end": v(-7.49, 13.05) * mm});
            skLineSegment(sketch, "E51.10.27", {"start": v(-3.84, 14.32) * mm, "end": v(-3.88, 14.4) * mm});
            skLineSegment(sketch, "E51.10.28", {"start": v(-7.39, 12.8) * mm, "end": v(-7.4, 12.84) * mm});
            skLineSegment(sketch, "E51.10.29", {"start": v(-7.38, 12.78) * mm, "end": v(-7.39, 12.8) * mm});
            skLineSegment(sketch, "E51.11.0", {"start": v(-10.65, 6.15) * mm, "end": v(-12.78, 7.38) * mm});
            skLineSegment(sketch, "E51.11.1", {"start": v(-12.45, 11.33) * mm, "end": v(-12.87, 11.42) * mm});
            skLineSegment(sketch, "E51.11.2", {"start": v(-8.7, 8.7) * mm, "end": v(-10.43, 10.43) * mm});
            skLineSegment(sketch, "E51.11.3", {"start": v(-12.08, 11.23) * mm, "end": v(-12.45, 11.33) * mm});
            skLineSegment(sketch, "E51.11.4", {"start": v(-13.98, 8.76) * mm, "end": v(-14.17, 9.1) * mm});
            skLineSegment(sketch, "E51.11.5", {"start": v(-14.17, 9.1) * mm, "end": v(-14.36, 9.48) * mm});
            skLineSegment(sketch, "E51.11.6", {"start": v(-11.75, 11.13) * mm, "end": v(-12.08, 11.23) * mm});
            skLineSegment(sketch, "E51.11.7", {"start": v(-13.32, 11.5) * mm, "end": v(-13.82, 11.55) * mm});
            skLineSegment(sketch, "E51.11.8", {"start": v(-11.45, 11.02) * mm, "end": v(-11.75, 11.13) * mm});
            skLineSegment(sketch, "E51.11.9", {"start": v(-14.55, 9.9) * mm, "end": v(-14.73, 10.36) * mm});
            skLineSegment(sketch, "E51.11.10", {"start": v(-12.87, 11.42) * mm, "end": v(-13.32, 11.5) * mm});
            skLineSegment(sketch, "E51.11.11", {"start": v(-13.79, 8.47) * mm, "end": v(-13.98, 8.76) * mm});
            skLineSegment(sketch, "E51.11.12", {"start": v(-14.36, 9.48) * mm, "end": v(-14.55, 9.9) * mm});
            skLineSegment(sketch, "E51.11.13", {"start": v(-10.8, 10.7) * mm, "end": v(-10.99, 10.8) * mm});
            skLineSegment(sketch, "E51.11.14", {"start": v(-10.99, 10.8) * mm, "end": v(-11.2, 10.9) * mm});
            skLineSegment(sketch, "E51.11.15", {"start": v(-11.2, 10.9) * mm, "end": v(-11.45, 11.02) * mm});
            skLineSegment(sketch, "E51.11.16", {"start": v(-13.43, 8) * mm, "end": v(-13.6, 8.21) * mm});
            skLineSegment(sketch, "E51.11.17", {"start": v(-13.27, 7.82) * mm, "end": v(-13.43, 8) * mm});
            skLineSegment(sketch, "E51.11.18", {"start": v(-13.6, 8.21) * mm, "end": v(-13.79, 8.47) * mm});
            skLineSegment(sketch, "E51.11.19", {"start": v(-10.67, 10.61) * mm, "end": v(-10.8, 10.7) * mm});
            skLineSegment(sketch, "E51.11.20", {"start": v(-10.56, 10.54) * mm, "end": v(-10.67, 10.61) * mm});
            skLineSegment(sketch, "E51.11.21", {"start": v(-13.13, 7.67) * mm, "end": v(-13.27, 7.82) * mm});
            skLineSegment(sketch, "E51.11.22", {"start": v(-13.01, 7.56) * mm, "end": v(-13.13, 7.67) * mm});
            skLineSegment(sketch, "E51.11.23", {"start": v(-12.84, 7.42) * mm, "end": v(-12.91, 7.47) * mm});
            skLineSegment(sketch, "E51.11.24", {"start": v(-10.43, 10.43) * mm, "end": v(-10.45, 10.45) * mm});
            skLineSegment(sketch, "E51.11.25", {"start": v(-10.45, 10.45) * mm, "end": v(-10.49, 10.48) * mm});
            skLineSegment(sketch, "E51.11.26", {"start": v(-12.91, 7.47) * mm, "end": v(-13.01, 7.56) * mm});
            skLineSegment(sketch, "E51.11.27", {"start": v(-10.49, 10.48) * mm, "end": v(-10.56, 10.54) * mm});
            skLineSegment(sketch, "E51.11.28", {"start": v(-12.8, 7.39) * mm, "end": v(-12.84, 7.42) * mm});
            skLineSegment(sketch, "E51.11.29", {"start": v(-12.78, 7.38) * mm, "end": v(-12.8, 7.39) * mm});
            skSolve(sketch);
        }
        {
            var Q0;
            {var subQ0=sQuery(id+"F1.wireOp",EDGE,"E0");var subQ27=makeQuery(id+"F1.imprint","INTERSECT",VERTEX,{"derivedFrom":[subQ0,sQuery(id+"F1.wireOp",EDGE,"E51.10.0")]});Q0=makeQuery(id+"F1.imprint","IMPRINT",FACE,{"disambiguationData":[TD([[makeQuery(id+"F1.imprint","IMPRINT",EDGE,{"disambiguationData":[TD([[subQ27,-1.0]])],"derivedFrom":subQ0}),1.0]])]});}
            var Q1;
            {var subQ0=sQuery(id+"F1.wireOp",EDGE,"E51.1.0");Q1=makeQuery(id+"F1.imprint","IMPRINT",FACE,{"disambiguationData":[TD([[makeQuery(id+"F1.imprint","IMPRINT",EDGE,{"derivedFrom":subQ0}),-1.0]])]});}
            var Q2;
            {var subQ7=sQuery(id+"F1.wireOp",EDGE,"E51.2.0");Q2=makeQuery(id+"F1.imprint","IMPRINT",FACE,{"disambiguationData":[TD([[makeQuery(id+"F1.imprint","IMPRINT",EDGE,{"derivedFrom":subQ7}),-1.0]])]});}
            var Q3;
            {var subQ8=sQuery(id+"F1.wireOp",EDGE,"E51.3.0");Q3=makeQuery(id+"F1.imprint","IMPRINT",FACE,{"disambiguationData":[TD([[makeQuery(id+"F1.imprint","IMPRINT",EDGE,{"derivedFrom":subQ8}),-1.0]])]});}
            var Q4;
            {var subQ2=sQuery(id+"F1.wireOp",EDGE,"E51.4.0");Q4=makeQuery(id+"F1.imprint","IMPRINT",FACE,{"disambiguationData":[TD([[makeQuery(id+"F1.imprint","IMPRINT",EDGE,{"derivedFrom":subQ2}),-1.0]])]});}
            var Q5;
            {var subQ8=sQuery(id+"F1.wireOp",EDGE,"E51.5.0");Q5=makeQuery(id+"F1.imprint","IMPRINT",FACE,{"disambiguationData":[TD([[makeQuery(id+"F1.imprint","IMPRINT",EDGE,{"derivedFrom":subQ8}),-1.0]])]});}
            var Q6;
            {var subQ3=sQuery(id+"F1.wireOp",EDGE,"E51.6.0");Q6=makeQuery(id+"F1.imprint","IMPRINT",FACE,{"disambiguationData":[TD([[makeQuery(id+"F1.imprint","IMPRINT",EDGE,{"derivedFrom":subQ3}),-1.0]])]});}
            var Q7;
            {var subQ0=sQuery(id+"F1.wireOp",EDGE,"E51.7.0");Q7=makeQuery(id+"F1.imprint","IMPRINT",FACE,{"disambiguationData":[TD([[makeQuery(id+"F1.imprint","IMPRINT",EDGE,{"derivedFrom":subQ0}),-1.0]])]});}
            var Q8;
            {var subQ5=sQuery(id+"F1.wireOp",EDGE,"E51.8.0");Q8=makeQuery(id+"F1.imprint","IMPRINT",FACE,{"disambiguationData":[TD([[makeQuery(id+"F1.imprint","IMPRINT",EDGE,{"derivedFrom":subQ5}),-1.0]])]});}
            var Q9;
            {var subQ1=sQuery(id+"F1.wireOp",EDGE,"E51.9.0");Q9=makeQuery(id+"F1.imprint","IMPRINT",FACE,{"disambiguationData":[TD([[makeQuery(id+"F1.imprint","IMPRINT",EDGE,{"derivedFrom":subQ1}),-1.0]])]});}
            var Q10;
            {var subQ5=sQuery(id+"F1.wireOp",EDGE,"E51.10.0");Q10=makeQuery(id+"F1.imprint","IMPRINT",FACE,{"disambiguationData":[TD([[makeQuery(id+"F1.imprint","IMPRINT",EDGE,{"derivedFrom":subQ5}),-1.0]])]});}
            var Q11;
            {var subQ8=sQuery(id+"F1.wireOp",EDGE,"E51.11.0");Q11=makeQuery(id+"F1.imprint","IMPRINT",FACE,{"disambiguationData":[TD([[makeQuery(id+"F1.imprint","IMPRINT",EDGE,{"derivedFrom":subQ8}),-1.0]])]});}
            var Q12;
            {var subQ2=sQuery(id+"F1.wireOp",EDGE,"E51.12.0");Q12=makeQuery(id+"F1.imprint","IMPRINT",FACE,{"disambiguationData":[TD([[makeQuery(id+"F1.imprint","IMPRINT",EDGE,{"derivedFrom":subQ2}),-1.0]])]});}
            var Q13;
            {var subQ3=sQuery(id+"F1.wireOp",EDGE,"E51.13.0");Q13=makeQuery(id+"F1.imprint","IMPRINT",FACE,{"disambiguationData":[TD([[makeQuery(id+"F1.imprint","IMPRINT",EDGE,{"derivedFrom":subQ3}),-1.0]])]});}
            var Q14;
            {var subQ0=sQuery(id+"F1.wireOp",EDGE,"E51.14.0");Q14=makeQuery(id+"F1.imprint","IMPRINT",FACE,{"disambiguationData":[TD([[makeQuery(id+"F1.imprint","IMPRINT",EDGE,{"derivedFrom":subQ0}),-1.0]])]});}
            var Q15;
            {var subQ6=sQuery(id+"F1.wireOp",EDGE,"E51.15.0");Q15=makeQuery(id+"F1.imprint","IMPRINT",FACE,{"disambiguationData":[TD([[makeQuery(id+"F1.imprint","IMPRINT",EDGE,{"derivedFrom":subQ6}),-1.0]])]});}
            var Q16;
            {var subQ5=sQuery(id+"F1.wireOp",EDGE,"E51.16.0");Q16=makeQuery(id+"F1.imprint","IMPRINT",FACE,{"disambiguationData":[TD([[makeQuery(id+"F1.imprint","IMPRINT",EDGE,{"derivedFrom":subQ5}),-1.0]])]});}
            var Q17;
            {var subQ7=sQuery(id+"F1.wireOp",EDGE,"E51.17.0");Q17=makeQuery(id+"F1.imprint","IMPRINT",FACE,{"disambiguationData":[TD([[makeQuery(id+"F1.imprint","IMPRINT",EDGE,{"derivedFrom":subQ7}),-1.0]])]});}
            var Q18;
            {var subQ5=sQuery(id+"F1.wireOp",EDGE,"E51.18.0");Q18=makeQuery(id+"F1.imprint","IMPRINT",FACE,{"disambiguationData":[TD([[makeQuery(id+"F1.imprint","IMPRINT",EDGE,{"derivedFrom":subQ5}),-1.0]])]});}
            var Q19;
            {var subQ8=sQuery(id+"F1.wireOp",EDGE,"E51.19.0");Q19=makeQuery(id+"F1.imprint","IMPRINT",FACE,{"disambiguationData":[TD([[makeQuery(id+"F1.imprint","IMPRINT",EDGE,{"derivedFrom":subQ8}),-1.0]])]});}
            var Q20;
            {var subQ8=sQuery(id+"F1.wireOp",EDGE,"E21");Q20=makeQuery(id+"F1.imprint","IMPRINT",FACE,{"disambiguationData":[TD([[makeQuery(id+"F1.imprint","IMPRINT",EDGE,{"derivedFrom":subQ8}),-1.0]])]});}
            extrude(context, id + "F2", {"entities" : qUnion([Q0, Q1, Q2, Q3, Q4, Q5, Q6, Q7, Q8, Q9, Q10, Q11, Q12, Q13, Q14, Q15, Q16, Q17, Q18, Q19, Q20]), "depth" : (getVariable(context, 'GearThickness')) * mm});
        }
        {
            var Q0;
            Q0=makeQuery(id+"F2.opExtrude","CAP_FACE",FACE,{"disambiguationData":[OSD([sQuery(id+"F1.wireOp",EDGE,"E0"),sQuery(id+"F1.wireOp",EDGE,"E3"),sQuery(id+"F1.wireOp",EDGE,"E21"),sQuery(id+"F1.wireOp",EDGE,"E22.MirrorCS"),sQuery(id+"F1.wireOp",EDGE,"E23"),sQuery(id+"F1.wireOp",EDGE,"E24"),sQuery(id+"F1.wireOp",EDGE,"E25"),sQuery(id+"F1.wireOp",EDGE,"E26"),sQuery(id+"F1.wireOp",EDGE,"E27"),sQuery(id+"F1.wireOp",EDGE,"E28"),sQuery(id+"F1.wireOp",EDGE,"E29"),sQuery(id+"F1.wireOp",EDGE,"E30"),sQuery(id+"F1.wireOp",EDGE,"E31"),sQuery(id+"F1.wireOp",EDGE,"E32"),sQuery(id+"F1.wireOp",EDGE,"E33"),sQuery(id+"F1.wireOp",EDGE,"E34"),sQuery(id+"F1.wireOp",EDGE,"E35"),sQuery(id+"F1.wireOp",EDGE,"E36"),sQuery(id+"F1.wireOp",EDGE,"E37.MirrorCS"),sQuery(id+"F1.wireOp",EDGE,"E38.MirrorCS"),sQuery(id+"F1.wireOp",EDGE,"E39.MirrorCS"),sQuery(id+"F1.wireOp",EDGE,"E40.MirrorCS"),sQuery(id+"F1.wireOp",EDGE,"E41.MirrorCS"),sQuery(id+"F1.wireOp",EDGE,"E42.MirrorCS"),sQuery(id+"F1.wireOp",EDGE,"E43.MirrorCS"),sQuery(id+"F1.wireOp",EDGE,"E44.MirrorCS"),sQuery(id+"F1.wireOp",EDGE,"E45.MirrorCS"),sQuery(id+"F1.wireOp",EDGE,"E46.MirrorCS"),sQuery(id+"F1.wireOp",EDGE,"E47.MirrorCS"),sQuery(id+"F1.wireOp",EDGE,"E48.MirrorCS"),sQuery(id+"F1.wireOp",EDGE,"E49.MirrorCS"),sQuery(id+"F1.wireOp",EDGE,"E50.MirrorCS"),sQuery(id+"F1.wireOp",EDGE,"E51.1.0"),sQuery(id+"F1.wireOp",EDGE,"E51.1.1"),sQuery(id+"F1.wireOp",EDGE,"E51.1.2"),sQuery(id+"F1.wireOp",EDGE,"E51.1.3"),sQuery(id+"F1.wireOp",EDGE,"E51.1.4"),sQuery(id+"F1.wireOp",EDGE,"E51.1.5"),sQuery(id+"F1.wireOp",EDGE,"E51.1.6"),sQuery(id+"F1.wireOp",EDGE,"E51.1.7"),sQuery(id+"F1.wireOp",EDGE,"E51.1.8"),sQuery(id+"F1.wireOp",EDGE,"E51.1.9"),sQuery(id+"F1.wireOp",EDGE,"E51.1.10"),sQuery(id+"F1.wireOp",EDGE,"E51.1.11"),sQuery(id+"F1.wireOp",EDGE,"E51.1.12"),sQuery(id+"F1.wireOp",EDGE,"E51.1.13"),sQuery(id+"F1.wireOp",EDGE,"E51.1.14"),sQuery(id+"F1.wireOp",EDGE,"E51.1.15"),sQuery(id+"F1.wireOp",EDGE,"E51.1.16"),sQuery(id+"F1.wireOp",EDGE,"E51.1.17"),sQuery(id+"F1.wireOp",EDGE,"E51.1.18"),sQuery(id+"F1.wireOp",EDGE,"E51.1.19"),sQuery(id+"F1.wireOp",EDGE,"E51.1.20"),sQuery(id+"F1.wireOp",EDGE,"E51.1.21"),sQuery(id+"F1.wireOp",EDGE,"E51.1.22"),sQuery(id+"F1.wireOp",EDGE,"E51.1.23"),sQuery(id+"F1.wireOp",EDGE,"E51.1.24"),sQuery(id+"F1.wireOp",EDGE,"E51.1.25"),sQuery(id+"F1.wireOp",EDGE,"E51.1.26"),sQuery(id+"F1.wireOp",EDGE,"E51.1.27"),sQuery(id+"F1.wireOp",EDGE,"E51.1.28"),sQuery(id+"F1.wireOp",EDGE,"E51.1.29"),sQuery(id+"F1.wireOp",EDGE,"E51.2.0"),sQuery(id+"F1.wireOp",EDGE,"E51.2.1"),sQuery(id+"F1.wireOp",EDGE,"E51.2.2"),sQuery(id+"F1.wireOp",EDGE,"E51.2.3"),sQuery(id+"F1.wireOp",EDGE,"E51.2.4"),sQuery(id+"F1.wireOp",EDGE,"E51.2.5"),sQuery(id+"F1.wireOp",EDGE,"E51.2.6"),sQuery(id+"F1.wireOp",EDGE,"E51.2.7"),sQuery(id+"F1.wireOp",EDGE,"E51.2.8"),sQuery(id+"F1.wireOp",EDGE,"E51.2.9"),sQuery(id+"F1.wireOp",EDGE,"E51.2.10"),sQuery(id+"F1.wireOp",EDGE,"E51.2.11"),sQuery(id+"F1.wireOp",EDGE,"E51.2.12"),sQuery(id+"F1.wireOp",EDGE,"E51.2.13"),sQuery(id+"F1.wireOp",EDGE,"E51.2.14"),sQuery(id+"F1.wireOp",EDGE,"E51.2.15"),sQuery(id+"F1.wireOp",EDGE,"E51.2.16"),sQuery(id+"F1.wireOp",EDGE,"E51.2.17"),sQuery(id+"F1.wireOp",EDGE,"E51.2.18"),sQuery(id+"F1.wireOp",EDGE,"E51.2.19"),sQuery(id+"F1.wireOp",EDGE,"E51.2.20"),sQuery(id+"F1.wireOp",EDGE,"E51.2.21"),sQuery(id+"F1.wireOp",EDGE,"E51.2.22"),sQuery(id+"F1.wireOp",EDGE,"E51.2.23"),sQuery(id+"F1.wireOp",EDGE,"E51.2.24"),sQuery(id+"F1.wireOp",EDGE,"E51.2.25"),sQuery(id+"F1.wireOp",EDGE,"E51.2.26"),sQuery(id+"F1.wireOp",EDGE,"E51.2.27"),sQuery(id+"F1.wireOp",EDGE,"E51.2.28"),sQuery(id+"F1.wireOp",EDGE,"E51.2.29"),sQuery(id+"F1.wireOp",EDGE,"E51.3.0"),sQuery(id+"F1.wireOp",EDGE,"E51.3.1"),sQuery(id+"F1.wireOp",EDGE,"E51.3.2"),sQuery(id+"F1.wireOp",EDGE,"E51.3.3"),sQuery(id+"F1.wireOp",EDGE,"E51.3.4"),sQuery(id+"F1.wireOp",EDGE,"E51.3.5"),sQuery(id+"F1.wireOp",EDGE,"E51.3.6"),sQuery(id+"F1.wireOp",EDGE,"E51.3.7"),sQuery(id+"F1.wireOp",EDGE,"E51.3.8"),sQuery(id+"F1.wireOp",EDGE,"E51.3.9"),sQuery(id+"F1.wireOp",EDGE,"E51.3.10"),sQuery(id+"F1.wireOp",EDGE,"E51.3.11"),sQuery(id+"F1.wireOp",EDGE,"E51.3.12"),sQuery(id+"F1.wireOp",EDGE,"E51.3.13"),sQuery(id+"F1.wireOp",EDGE,"E51.3.14"),sQuery(id+"F1.wireOp",EDGE,"E51.3.15"),sQuery(id+"F1.wireOp",EDGE,"E51.3.16"),sQuery(id+"F1.wireOp",EDGE,"E51.3.17"),sQuery(id+"F1.wireOp",EDGE,"E51.3.18"),sQuery(id+"F1.wireOp",EDGE,"E51.3.19"),sQuery(id+"F1.wireOp",EDGE,"E51.3.20"),sQuery(id+"F1.wireOp",EDGE,"E51.3.21"),sQuery(id+"F1.wireOp",EDGE,"E51.3.22"),sQuery(id+"F1.wireOp",EDGE,"E51.3.23"),sQuery(id+"F1.wireOp",EDGE,"E51.3.24"),sQuery(id+"F1.wireOp",EDGE,"E51.3.25"),sQuery(id+"F1.wireOp",EDGE,"E51.3.26"),sQuery(id+"F1.wireOp",EDGE,"E51.3.27"),sQuery(id+"F1.wireOp",EDGE,"E51.3.28"),sQuery(id+"F1.wireOp",EDGE,"E51.3.29"),sQuery(id+"F1.wireOp",EDGE,"E51.4.0"),sQuery(id+"F1.wireOp",EDGE,"E51.4.1"),sQuery(id+"F1.wireOp",EDGE,"E51.4.2"),sQuery(id+"F1.wireOp",EDGE,"E51.4.3"),sQuery(id+"F1.wireOp",EDGE,"E51.4.4"),sQuery(id+"F1.wireOp",EDGE,"E51.4.5"),sQuery(id+"F1.wireOp",EDGE,"E51.4.6"),sQuery(id+"F1.wireOp",EDGE,"E51.4.7"),sQuery(id+"F1.wireOp",EDGE,"E51.4.8"),sQuery(id+"F1.wireOp",EDGE,"E51.4.9"),sQuery(id+"F1.wireOp",EDGE,"E51.4.10"),sQuery(id+"F1.wireOp",EDGE,"E51.4.11"),sQuery(id+"F1.wireOp",EDGE,"E51.4.12"),sQuery(id+"F1.wireOp",EDGE,"E51.4.13"),sQuery(id+"F1.wireOp",EDGE,"E51.4.14"),sQuery(id+"F1.wireOp",EDGE,"E51.4.15"),sQuery(id+"F1.wireOp",EDGE,"E51.4.16"),sQuery(id+"F1.wireOp",EDGE,"E51.4.17"),sQuery(id+"F1.wireOp",EDGE,"E51.4.18"),sQuery(id+"F1.wireOp",EDGE,"E51.4.19"),sQuery(id+"F1.wireOp",EDGE,"E51.4.20"),sQuery(id+"F1.wireOp",EDGE,"E51.4.21"),sQuery(id+"F1.wireOp",EDGE,"E51.4.22"),sQuery(id+"F1.wireOp",EDGE,"E51.4.23"),sQuery(id+"F1.wireOp",EDGE,"E51.4.24"),sQuery(id+"F1.wireOp",EDGE,"E51.4.25"),sQuery(id+"F1.wireOp",EDGE,"E51.4.26"),sQuery(id+"F1.wireOp",EDGE,"E51.4.27"),sQuery(id+"F1.wireOp",EDGE,"E51.4.28"),sQuery(id+"F1.wireOp",EDGE,"E51.4.29"),sQuery(id+"F1.wireOp",EDGE,"E51.5.0"),sQuery(id+"F1.wireOp",EDGE,"E51.5.1"),sQuery(id+"F1.wireOp",EDGE,"E51.5.2"),sQuery(id+"F1.wireOp",EDGE,"E51.5.3"),sQuery(id+"F1.wireOp",EDGE,"E51.5.4"),sQuery(id+"F1.wireOp",EDGE,"E51.5.5"),sQuery(id+"F1.wireOp",EDGE,"E51.5.6"),sQuery(id+"F1.wireOp",EDGE,"E51.5.7"),sQuery(id+"F1.wireOp",EDGE,"E51.5.8"),sQuery(id+"F1.wireOp",EDGE,"E51.5.9"),sQuery(id+"F1.wireOp",EDGE,"E51.5.10"),sQuery(id+"F1.wireOp",EDGE,"E51.5.11"),sQuery(id+"F1.wireOp",EDGE,"E51.5.12"),sQuery(id+"F1.wireOp",EDGE,"E51.5.13"),sQuery(id+"F1.wireOp",EDGE,"E51.5.14"),sQuery(id+"F1.wireOp",EDGE,"E51.5.15"),sQuery(id+"F1.wireOp",EDGE,"E51.5.16"),sQuery(id+"F1.wireOp",EDGE,"E51.5.17"),sQuery(id+"F1.wireOp",EDGE,"E51.5.18"),sQuery(id+"F1.wireOp",EDGE,"E51.5.19"),sQuery(id+"F1.wireOp",EDGE,"E51.5.20"),sQuery(id+"F1.wireOp",EDGE,"E51.5.21"),sQuery(id+"F1.wireOp",EDGE,"E51.5.22"),sQuery(id+"F1.wireOp",EDGE,"E51.5.23"),sQuery(id+"F1.wireOp",EDGE,"E51.5.24"),sQuery(id+"F1.wireOp",EDGE,"E51.5.25"),sQuery(id+"F1.wireOp",EDGE,"E51.5.26"),sQuery(id+"F1.wireOp",EDGE,"E51.5.27"),sQuery(id+"F1.wireOp",EDGE,"E51.5.28"),sQuery(id+"F1.wireOp",EDGE,"E51.5.29"),sQuery(id+"F1.wireOp",EDGE,"E51.6.0"),sQuery(id+"F1.wireOp",EDGE,"E51.6.1"),sQuery(id+"F1.wireOp",EDGE,"E51.6.2"),sQuery(id+"F1.wireOp",EDGE,"E51.6.3"),sQuery(id+"F1.wireOp",EDGE,"E51.6.4"),sQuery(id+"F1.wireOp",EDGE,"E51.6.5"),sQuery(id+"F1.wireOp",EDGE,"E51.6.6"),sQuery(id+"F1.wireOp",EDGE,"E51.6.7"),sQuery(id+"F1.wireOp",EDGE,"E51.6.8"),sQuery(id+"F1.wireOp",EDGE,"E51.6.9"),sQuery(id+"F1.wireOp",EDGE,"E51.6.10"),sQuery(id+"F1.wireOp",EDGE,"E51.6.11"),sQuery(id+"F1.wireOp",EDGE,"E51.6.12"),sQuery(id+"F1.wireOp",EDGE,"E51.6.13"),sQuery(id+"F1.wireOp",EDGE,"E51.6.14"),sQuery(id+"F1.wireOp",EDGE,"E51.6.15"),sQuery(id+"F1.wireOp",EDGE,"E51.6.16"),sQuery(id+"F1.wireOp",EDGE,"E51.6.17"),sQuery(id+"F1.wireOp",EDGE,"E51.6.18"),sQuery(id+"F1.wireOp",EDGE,"E51.6.19"),sQuery(id+"F1.wireOp",EDGE,"E51.6.20"),sQuery(id+"F1.wireOp",EDGE,"E51.6.21"),sQuery(id+"F1.wireOp",EDGE,"E51.6.22"),sQuery(id+"F1.wireOp",EDGE,"E51.6.23"),sQuery(id+"F1.wireOp",EDGE,"E51.6.24"),sQuery(id+"F1.wireOp",EDGE,"E51.6.25"),sQuery(id+"F1.wireOp",EDGE,"E51.6.26"),sQuery(id+"F1.wireOp",EDGE,"E51.6.27"),sQuery(id+"F1.wireOp",EDGE,"E51.6.28"),sQuery(id+"F1.wireOp",EDGE,"E51.6.29"),sQuery(id+"F1.wireOp",EDGE,"E51.7.0"),sQuery(id+"F1.wireOp",EDGE,"E51.7.1"),sQuery(id+"F1.wireOp",EDGE,"E51.7.2"),sQuery(id+"F1.wireOp",EDGE,"E51.7.3"),sQuery(id+"F1.wireOp",EDGE,"E51.7.4"),sQuery(id+"F1.wireOp",EDGE,"E51.7.5"),sQuery(id+"F1.wireOp",EDGE,"E51.7.6"),sQuery(id+"F1.wireOp",EDGE,"E51.7.7"),sQuery(id+"F1.wireOp",EDGE,"E51.7.8"),sQuery(id+"F1.wireOp",EDGE,"E51.7.9"),sQuery(id+"F1.wireOp",EDGE,"E51.7.10"),sQuery(id+"F1.wireOp",EDGE,"E51.7.11"),sQuery(id+"F1.wireOp",EDGE,"E51.7.12"),sQuery(id+"F1.wireOp",EDGE,"E51.7.13"),sQuery(id+"F1.wireOp",EDGE,"E51.7.14"),sQuery(id+"F1.wireOp",EDGE,"E51.7.15"),sQuery(id+"F1.wireOp",EDGE,"E51.7.16"),sQuery(id+"F1.wireOp",EDGE,"E51.7.17"),sQuery(id+"F1.wireOp",EDGE,"E51.7.18"),sQuery(id+"F1.wireOp",EDGE,"E51.7.19"),sQuery(id+"F1.wireOp",EDGE,"E51.7.20"),sQuery(id+"F1.wireOp",EDGE,"E51.7.21"),sQuery(id+"F1.wireOp",EDGE,"E51.7.22"),sQuery(id+"F1.wireOp",EDGE,"E51.7.23"),sQuery(id+"F1.wireOp",EDGE,"E51.7.24"),sQuery(id+"F1.wireOp",EDGE,"E51.7.25"),sQuery(id+"F1.wireOp",EDGE,"E51.7.26"),sQuery(id+"F1.wireOp",EDGE,"E51.7.27"),sQuery(id+"F1.wireOp",EDGE,"E51.7.28"),sQuery(id+"F1.wireOp",EDGE,"E51.7.29"),sQuery(id+"F1.wireOp",EDGE,"E51.8.0"),sQuery(id+"F1.wireOp",EDGE,"E51.8.1"),sQuery(id+"F1.wireOp",EDGE,"E51.8.2"),sQuery(id+"F1.wireOp",EDGE,"E51.8.3"),sQuery(id+"F1.wireOp",EDGE,"E51.8.4"),sQuery(id+"F1.wireOp",EDGE,"E51.8.5"),sQuery(id+"F1.wireOp",EDGE,"E51.8.6"),sQuery(id+"F1.wireOp",EDGE,"E51.8.7"),sQuery(id+"F1.wireOp",EDGE,"E51.8.8"),sQuery(id+"F1.wireOp",EDGE,"E51.8.9"),sQuery(id+"F1.wireOp",EDGE,"E51.8.10"),sQuery(id+"F1.wireOp",EDGE,"E51.8.11"),sQuery(id+"F1.wireOp",EDGE,"E51.8.12"),sQuery(id+"F1.wireOp",EDGE,"E51.8.13"),sQuery(id+"F1.wireOp",EDGE,"E51.8.14"),sQuery(id+"F1.wireOp",EDGE,"E51.8.15"),sQuery(id+"F1.wireOp",EDGE,"E51.8.16"),sQuery(id+"F1.wireOp",EDGE,"E51.8.17"),sQuery(id+"F1.wireOp",EDGE,"E51.8.18"),sQuery(id+"F1.wireOp",EDGE,"E51.8.19"),sQuery(id+"F1.wireOp",EDGE,"E51.8.20"),sQuery(id+"F1.wireOp",EDGE,"E51.8.21"),sQuery(id+"F1.wireOp",EDGE,"E51.8.22"),sQuery(id+"F1.wireOp",EDGE,"E51.8.23"),sQuery(id+"F1.wireOp",EDGE,"E51.8.24"),sQuery(id+"F1.wireOp",EDGE,"E51.8.25"),sQuery(id+"F1.wireOp",EDGE,"E51.8.26"),sQuery(id+"F1.wireOp",EDGE,"E51.8.27"),sQuery(id+"F1.wireOp",EDGE,"E51.8.28"),sQuery(id+"F1.wireOp",EDGE,"E51.8.29"),sQuery(id+"F1.wireOp",EDGE,"E51.9.0"),sQuery(id+"F1.wireOp",EDGE,"E51.9.1"),sQuery(id+"F1.wireOp",EDGE,"E51.9.2"),sQuery(id+"F1.wireOp",EDGE,"E51.9.3"),sQuery(id+"F1.wireOp",EDGE,"E51.9.4"),sQuery(id+"F1.wireOp",EDGE,"E51.9.5"),sQuery(id+"F1.wireOp",EDGE,"E51.9.6"),sQuery(id+"F1.wireOp",EDGE,"E51.9.7"),sQuery(id+"F1.wireOp",EDGE,"E51.9.8"),sQuery(id+"F1.wireOp",EDGE,"E51.9.9"),sQuery(id+"F1.wireOp",EDGE,"E51.9.10"),sQuery(id+"F1.wireOp",EDGE,"E51.9.11"),sQuery(id+"F1.wireOp",EDGE,"E51.9.12"),sQuery(id+"F1.wireOp",EDGE,"E51.9.13"),sQuery(id+"F1.wireOp",EDGE,"E51.9.14"),sQuery(id+"F1.wireOp",EDGE,"E51.9.15"),sQuery(id+"F1.wireOp",EDGE,"E51.9.16"),sQuery(id+"F1.wireOp",EDGE,"E51.9.17"),sQuery(id+"F1.wireOp",EDGE,"E51.9.18"),sQuery(id+"F1.wireOp",EDGE,"E51.9.19"),sQuery(id+"F1.wireOp",EDGE,"E51.9.20"),sQuery(id+"F1.wireOp",EDGE,"E51.9.21"),sQuery(id+"F1.wireOp",EDGE,"E51.9.22"),sQuery(id+"F1.wireOp",EDGE,"E51.9.23"),sQuery(id+"F1.wireOp",EDGE,"E51.9.24"),sQuery(id+"F1.wireOp",EDGE,"E51.9.25"),sQuery(id+"F1.wireOp",EDGE,"E51.9.26"),sQuery(id+"F1.wireOp",EDGE,"E51.9.27"),sQuery(id+"F1.wireOp",EDGE,"E51.9.28"),sQuery(id+"F1.wireOp",EDGE,"E51.9.29"),sQuery(id+"F1.wireOp",EDGE,"E51.10.0"),sQuery(id+"F1.wireOp",EDGE,"E51.10.1"),sQuery(id+"F1.wireOp",EDGE,"E51.10.2"),sQuery(id+"F1.wireOp",EDGE,"E51.10.3"),sQuery(id+"F1.wireOp",EDGE,"E51.10.4"),sQuery(id+"F1.wireOp",EDGE,"E51.10.5"),sQuery(id+"F1.wireOp",EDGE,"E51.10.6"),sQuery(id+"F1.wireOp",EDGE,"E51.10.7"),sQuery(id+"F1.wireOp",EDGE,"E51.10.8"),sQuery(id+"F1.wireOp",EDGE,"E51.10.9"),sQuery(id+"F1.wireOp",EDGE,"E51.10.10"),sQuery(id+"F1.wireOp",EDGE,"E51.10.11"),sQuery(id+"F1.wireOp",EDGE,"E51.10.12"),sQuery(id+"F1.wireOp",EDGE,"E51.10.13"),sQuery(id+"F1.wireOp",EDGE,"E51.10.14"),sQuery(id+"F1.wireOp",EDGE,"E51.10.15"),sQuery(id+"F1.wireOp",EDGE,"E51.10.16"),sQuery(id+"F1.wireOp",EDGE,"E51.10.17"),sQuery(id+"F1.wireOp",EDGE,"E51.10.18"),sQuery(id+"F1.wireOp",EDGE,"E51.10.19"),sQuery(id+"F1.wireOp",EDGE,"E51.10.20"),sQuery(id+"F1.wireOp",EDGE,"E51.10.21"),sQuery(id+"F1.wireOp",EDGE,"E51.10.22"),sQuery(id+"F1.wireOp",EDGE,"E51.10.23"),sQuery(id+"F1.wireOp",EDGE,"E51.10.24"),sQuery(id+"F1.wireOp",EDGE,"E51.10.25"),sQuery(id+"F1.wireOp",EDGE,"E51.10.26"),sQuery(id+"F1.wireOp",EDGE,"E51.10.27"),sQuery(id+"F1.wireOp",EDGE,"E51.10.28"),sQuery(id+"F1.wireOp",EDGE,"E51.10.29"),sQuery(id+"F1.wireOp",EDGE,"E51.11.0"),sQuery(id+"F1.wireOp",EDGE,"E51.11.1"),sQuery(id+"F1.wireOp",EDGE,"E51.11.2"),sQuery(id+"F1.wireOp",EDGE,"E51.11.3"),sQuery(id+"F1.wireOp",EDGE,"E51.11.4"),sQuery(id+"F1.wireOp",EDGE,"E51.11.5"),sQuery(id+"F1.wireOp",EDGE,"E51.11.6"),sQuery(id+"F1.wireOp",EDGE,"E51.11.7"),sQuery(id+"F1.wireOp",EDGE,"E51.11.8"),sQuery(id+"F1.wireOp",EDGE,"E51.11.9"),sQuery(id+"F1.wireOp",EDGE,"E51.11.10"),sQuery(id+"F1.wireOp",EDGE,"E51.11.11"),sQuery(id+"F1.wireOp",EDGE,"E51.11.12"),sQuery(id+"F1.wireOp",EDGE,"E51.11.13"),sQuery(id+"F1.wireOp",EDGE,"E51.11.14"),sQuery(id+"F1.wireOp",EDGE,"E51.11.15"),sQuery(id+"F1.wireOp",EDGE,"E51.11.16"),sQuery(id+"F1.wireOp",EDGE,"E51.11.17"),sQuery(id+"F1.wireOp",EDGE,"E51.11.18"),sQuery(id+"F1.wireOp",EDGE,"E51.11.19"),sQuery(id+"F1.wireOp",EDGE,"E51.11.20"),sQuery(id+"F1.wireOp",EDGE,"E51.11.21"),sQuery(id+"F1.wireOp",EDGE,"E51.11.22"),sQuery(id+"F1.wireOp",EDGE,"E51.11.23"),sQuery(id+"F1.wireOp",EDGE,"E51.11.24"),sQuery(id+"F1.wireOp",EDGE,"E51.11.25"),sQuery(id+"F1.wireOp",EDGE,"E51.11.26"),sQuery(id+"F1.wireOp",EDGE,"E51.11.27"),sQuery(id+"F1.wireOp",EDGE,"E51.11.28"),sQuery(id+"F1.wireOp",EDGE,"E51.11.29")])],"isStart":true});
            var sketch = newSketch(context, id + "F3", { "sketchPlane" : qUnion([Q0])});
            skCircle(sketch, "E52", {"center": v(0, 0) * mm, "radius": 5 * mm});
            skSolve(sketch);
        }
        {
            var Q0;
            Q0=makeQuery(id+"F3.imprint","IMPRINT",FACE,{"disambiguationData":[TD([[makeQuery(id+"F3.imprint","IMPRINT",EDGE,{"derivedFrom":sQuery(id+"F3.wireOp",EDGE,"E52")}),1.0]])]});
            var Q1;
            Q1=sQuery(id+"F3.wireOp",EDGE,"E52");
            extrude(context, id + "F4", {"entities" : qUnion([Q0]), "operationType" : NewBodyOperationType.REMOVE, "surfaceEntities" : qUnion([Q1]), "endBound" : BoundingType.THROUGH_ALL, "oppositeDirection" : true, "depth" : 25 * mm});
        }
    });
